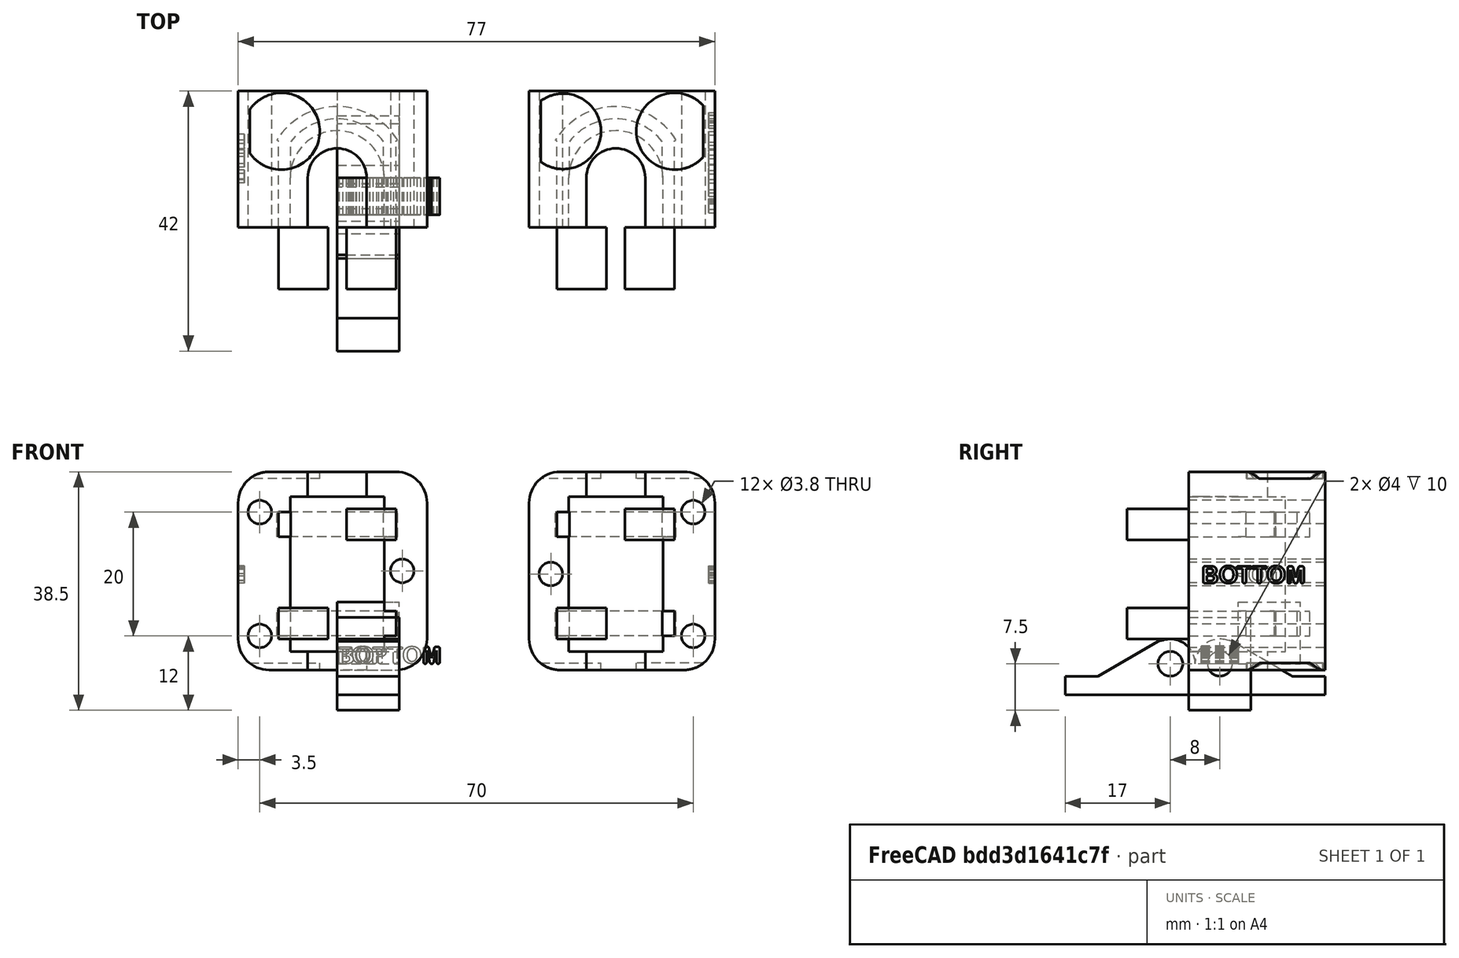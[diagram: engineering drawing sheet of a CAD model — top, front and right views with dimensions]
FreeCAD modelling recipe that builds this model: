
FCSTD DOCUMENT  (FreeCAD 0.16R6712 (Git))
Label: ParkingNozzleSliderIron
License: All rights reserved
LicenseURL: http://en.wikipedia.org/wiki/All_rights_reserved
objects: Part::Cylinder×51, Part::Box×26, Part::MultiFuse×26, Part::Cut×17, Part::Feature×3, Part::Part2DObjectPython×2, Part::Extrusion×2
note: 127 computed .brp shape members not serialized (recipe doc carries the construction recipe); baked Part::Feature solids carry a one-line shape summary decoded from their .brp

FEATURE [Part::Box] Box  label="Würfel"
  Height = 10
  Length = 10
  Width = 10
FEATURE [Part::Cylinder] Cylinder001  label="RJ4JP"
  Angle = 360
  Height = 25
  Placement = pos=(0,0,-0.5) rot=(0,0,1;0rad)
  Radius = 7.6
FEATURE [Part::Cylinder] Cylinder002  label="LinearStange8mm"
  Angle = 360
  Height = 44
  Placement = pos=(0,0,-10) rot=(0,0,1;0rad)
  Radius = 4.5
FEATURE [Part::Cylinder] Cylinder003  label="LinearSpacer9mm"
  Angle = 360
  Height = 34
  Placement = pos=(0,0,-5) rot=(0,0,1;0rad)
  Radius = 4.75
FEATURE [Part::MultiFuse] Fusion  label="GleitlagerAusspahrung"
  Shapes = -> [Cylinder001,Cylinder003,Cylinder002]
FEATURE [Part::Cylinder] Cylinder004  label="Zylinder001"
  Angle = 116
  Height = 4
  Placement = pos=(0,0,0) rot=(0,0,1;0.558505rad)
  Radius = 11.5
FEATURE [Part::Cylinder] Cylinder005  label="Zylinder002"
  Angle = 116
  Height = 4
  Placement = pos=(0,0,0) rot=(0,0,1;0.558505rad)
  Radius = 9.5
FEATURE [Part::Cut] Cut
  Base = -> Cylinder004
  Tool = -> Cylinder005
FEATURE [Part::Box] Box001  label="Würfel001"
  Height = 4
  Length = 2
  Placement = pos=(-9.5,-11,0) rot=(0,0,1;0rad)
  Width = 17
FEATURE [Part::Box] Box002  label="Würfel002"
  Height = 4
  Length = 2
  Placement = pos=(7.5,-11,0) rot=(0,0,1;0rad)
  Width = 17
FEATURE [Part::MultiFuse] Fusion001  label="KabelbinderAusspahrung002"
  Placement = pos=(0,0,18) rot=(0,0,1;0rad)
  Shapes = -> [Cut,Box002,Box001]
FEATURE [Part::Box] Box009  label="Würfel009"
  Height = 15
  Length = 10
  Placement = pos=(0,-8,-7.5) rot=(0,0,1;0rad)
  Width = 10
FEATURE [Part::Cylinder] Cylinder014  label="Zylinder008"
  Angle = 116
  Height = 4
  Placement = pos=(0,0,0) rot=(0,0,1;0.558505rad)
  Radius = 11.5
FEATURE [Part::Cylinder] Cylinder015  label="Zylinder009"
  Angle = 116
  Height = 4
  Placement = pos=(0,0,0) rot=(0,0,1;0.558505rad)
  Radius = 9.5
FEATURE [Part::Cut] Cut004
  Base = -> Cylinder014
  Tool = -> Cylinder015
FEATURE [Part::Box] Box010  label="Würfel010"
  Height = 4
  Length = 2
  Placement = pos=(-9.5,-11,0) rot=(0,0,1;0rad)
  Width = 17
FEATURE [Part::Box] Box011  label="Würfel011"
  Height = 4
  Length = 2
  Placement = pos=(7.5,-11,0) rot=(0,0,1;0rad)
  Width = 17
FEATURE [Part::MultiFuse] Fusion008  label="KabelbinderAusspahrung005"
  Placement = pos=(0,0,2) rot=(0,0,1;0rad)
  Shapes = -> [Cut004,Box011,Box010]
FEATURE [Part::Box] Box016  label="Block_A"
  Height = 32
  Length = 30.5
  Placement = pos=(-16,-8,-1) rot=(0,0,1;0rad)
  Width = 22
FEATURE [Part::Box] Box017  label="Würfel017"
  Height = 44
  Length = 9.5
  Placement = pos=(-4.75,-11,-10) rot=(0,0,1;0rad)
  Width = 11
FEATURE [Part::Box] Box018  label="Würfel018"
  Height = 25
  Length = 15.2
  Placement = pos=(-7.6,-11,-0.5) rot=(0,0,1;0rad)
  Width = 11
FEATURE [Part::MultiFuse] Fusion014  label="Schacht"
  Shapes = -> [Box017,Box018]
FEATURE [Part::MultiFuse] Fusion015  label="RJ4JP_Cut_Full_A"
  Shapes = -> [Fusion,Fusion001,Fusion008,Fusion014]
FEATURE [Part::Cylinder] Cylinder016  label="RJ4JP001"
  Angle = 360
  Height = 25
  Placement = pos=(0,0,-0.5) rot=(0,0,1;0rad)
  Radius = 7.6
FEATURE [Part::Cylinder] Cylinder017  label="LinearStange8mm001"
  Angle = 360
  Height = 44
  Placement = pos=(0,0,-10) rot=(0,0,1;0rad)
  Radius = 4.5
FEATURE [Part::Cylinder] Cylinder018  label="LinearSpacer9mm001"
  Angle = 360
  Height = 34
  Placement = pos=(0,0,-5) rot=(0,0,1;0rad)
  Radius = 4.75
FEATURE [Part::MultiFuse] Fusion016  label="GleitlagerAusspahrung001"
  Shapes = -> [Cylinder016,Cylinder018,Cylinder017]
FEATURE [Part::Cylinder] Cylinder019  label="Zylinder010"
  Angle = 116
  Height = 4
  Placement = pos=(0,0,0) rot=(0,0,1;0.558505rad)
  Radius = 11.5
FEATURE [Part::Cylinder] Cylinder020  label="Zylinder011"
  Angle = 116
  Height = 4
  Placement = pos=(0,0,0) rot=(0,0,1;0.558505rad)
  Radius = 9.5
FEATURE [Part::Cut] Cut005
  Base = -> Cylinder019
  Tool = -> Cylinder020
FEATURE [Part::Box] Box019  label="Würfel019"
  Height = 4
  Length = 2
  Placement = pos=(-9.5,-11,0) rot=(0,0,1;0rad)
  Width = 17
FEATURE [Part::Box] Box020  label="Würfel020"
  Height = 4
  Length = 2
  Placement = pos=(7.5,-11,0) rot=(0,0,1;0rad)
  Width = 17
FEATURE [Part::MultiFuse] Fusion017  label="KabelbinderAusspahrung006"
  Placement = pos=(0,0,18) rot=(0,0,1;0rad)
  Shapes = -> [Cut005,Box020,Box019]
FEATURE [Part::Cylinder] Cylinder021  label="Zylinder012"
  Angle = 116
  Height = 4
  Placement = pos=(0,0,0) rot=(0,0,1;0.558505rad)
  Radius = 11.5
FEATURE [Part::Cylinder] Cylinder022  label="Zylinder013"
  Angle = 116
  Height = 4
  Placement = pos=(0,0,0) rot=(0,0,1;0.558505rad)
  Radius = 9.5
FEATURE [Part::Cut] Cut006
  Base = -> Cylinder021
  Tool = -> Cylinder022
FEATURE [Part::Box] Box021  label="Würfel021"
  Height = 4
  Length = 2
  Placement = pos=(-9.5,-11,0) rot=(0,0,1;0rad)
  Width = 17
FEATURE [Part::Box] Box022  label="Würfel022"
  Height = 4
  Length = 2
  Placement = pos=(7.5,-11,0) rot=(0,0,1;0rad)
  Width = 17
FEATURE [Part::MultiFuse] Fusion018  label="KabelbinderAusspahrung007"
  Placement = pos=(0,0,2) rot=(0,0,1;0rad)
  Shapes = -> [Cut006,Box022,Box021]
FEATURE [Part::Box] Box023  label="Würfel023"
  Height = 44
  Length = 9.5
  Placement = pos=(-4.75,-11,-10) rot=(0,0,1;0rad)
  Width = 11
FEATURE [Part::Box] Box024  label="Würfel024"
  Height = 25
  Length = 15.2
  Placement = pos=(-7.6,-11,-0.5) rot=(0,0,1;0rad)
  Width = 11
FEATURE [Part::MultiFuse] Fusion019  label="Schacht001"
  Shapes = -> [Box023,Box024]
FEATURE [Part::MultiFuse] Fusion020  label="RJ4JP_Cut_Full_B"
  Placement = pos=(45,0,0) rot=(0,0,1;0rad)
  Shapes = -> [Fusion016,Fusion017,Fusion018,Fusion019]
FEATURE [Part::MultiFuse] Fusion021  label="X_RJ4JP_Cut"
  Placement = pos=(0,0,2.5) rot=(0,0,1;0rad)
  Shapes = -> [Fusion015,Fusion020]
FEATURE [Part::Box] Box025  label="Block_B"
  Height = 32
  Length = 30
  Placement = pos=(31,-8,-1) rot=(0,0,1;0rad)
  Width = 22
FEATURE [Part::MultiFuse] Fusion022  label="GleitBlock"
  Shapes = -> [Box016,Box025]
FEATURE [Part::Cut] Cut007  label="GleitBloecke"
  Base = -> Fusion022
  Tool = -> Fusion021
FEATURE [Part::Cylinder] Cylinder025  label="Zylinder016"
  Angle = 360
  Height = 10
  Radius = 2
FEATURE [Part::Cylinder] Cylinder026  label="Zylinder017"
  Angle = 360
  Height = 10
  Radius = 4
FEATURE [Part::Cut] Cut009
  Base = -> Cylinder026
  Placement = pos=(0,-11,0) rot=(0,0,1;0rad)
  Tool = -> Cylinder025
FEATURE [Part::Box] Box028  label="Würfel027"
  Height = 10
  Length = 3
  Placement = pos=(2,-28,0) rot=(0,0,1;0rad)
  Width = 22
FEATURE [Part::Box] Box029  label="Würfel028"
  Height = 10
  Length = 1
  Placement = pos=(3.9,-26,0) rot=(0,0,1;0.523599rad)
  Width = 15
FEATURE [Part::Box] Box030  label="Würfel029"
  Height = 10
  Length = 3.3
  Placement = pos=(2,-21.5,0) rot=(0,0,1;0.523599rad)
  Width = 8
FEATURE [Part::Cylinder] Cylinder027  label="Zylinder018"
  Angle = 360
  Height = 10
  Placement = pos=(2,-15,0) rot=(0,0,1;0rad)
  Radius = 2
FEATURE [Part::Cylinder] Cylinder028  label="Zylinder019"
  Angle = 360
  Height = 10
  Placement = pos=(-2.73,-12.5,0) rot=(0,0,1;0rad)
  Radius = 1
FEATURE [Part::MultiFuse] Fusion023
  Shapes = -> [Cut009,Cylinder027,Cylinder028,Box028,Box029,Box030]
FEATURE [Part::Cylinder] Cylinder029  label="Zylinder020"
  Angle = 360
  Height = 10
  Radius = 2
FEATURE [Part::Cylinder] Cylinder030  label="Zylinder021"
  Angle = 360
  Height = 10
  Radius = 4
FEATURE [Part::Cut] Cut010
  Base = -> Cylinder030
  Placement = pos=(0,-11,0) rot=(0,0,1;0rad)
  Tool = -> Cylinder029
FEATURE [Part::Box] Box031  label="Würfel030"
  Height = 10
  Length = 3
  Placement = pos=(2,-28,0) rot=(0,0,1;0rad)
  Width = 20
FEATURE [Part::Box] Box032  label="Würfel031"
  Height = 10
  Length = 1
  Placement = pos=(3.9,-26,0) rot=(0,0,1;0.523599rad)
  Width = 15
FEATURE [Part::Box] Box033  label="Würfel032"
  Height = 10
  Length = 3.3
  Placement = pos=(2,-21.5,0) rot=(0,0,1;0.523599rad)
  Width = 8
FEATURE [Part::Cylinder] Cylinder031  label="Zylinder022"
  Angle = 360
  Height = 10
  Placement = pos=(2,-15,0) rot=(0,0,1;0rad)
  Radius = 2
FEATURE [Part::Cylinder] Cylinder032  label="Zylinder023"
  Angle = 360
  Height = 10
  Placement = pos=(-2.73,-12.5,0) rot=(0,0,1;0rad)
  Radius = 1
FEATURE [Part::MultiFuse] Fusion024
  Placement = pos=(0,-14,10) rot=(1,0,0;3.14159rad)
  Shapes = -> [Cut010,Cylinder031,Cylinder032,Box031,Box032,Box033]
FEATURE [Part::MultiFuse] Fusion025
  Shapes = -> [Fusion023,Fusion024]
FEATURE [Part::Cylinder] Cylinder033  label="Zylinder024"
  Angle = 360
  Height = 10
  Placement = pos=(2,-7,0) rot=(0,0,1;0rad)
  Radius = 2
FEATURE [Part::MultiFuse] Fusion026
  Placement = pos=(0,0,0) rot=(0,1,0;1.5708rad)
  Shapes = -> [Fusion025,Cylinder033]
FEATURE [Part::Cylinder] Cylinder034  label="Zylinder025"
  Angle = 360
  Height = 26
  Placement = pos=(-13,16,4.5) rot=(1,0,0;1.5708rad)
  Radius = 1.9
FEATURE [Part::Cylinder] Cylinder035  label="Zylinder026"
  Angle = 360
  Height = 26
  Placement = pos=(-13,16,24.5) rot=(1,0,0;1.5708rad)
  Radius = 1.9
FEATURE [Part::Cylinder] Cylinder036  label="Zylinder027"
  Angle = 360
  Height = 26
  Placement = pos=(10.5,16,15) rot=(1,0,0;1.5708rad)
  Radius = 1.9
FEATURE [Part::MultiFuse] Fusion026003
  Placement = pos=(0.5,0,0) rot=(0,0,1;0rad)
  Shapes = -> [Cylinder034,Cylinder035]
FEATURE [Part::Cylinder] Cylinder037  label="Zylinder028"
  Angle = 360
  Height = 26
  Placement = pos=(-13,16,4.5) rot=(1,0,0;1.5708rad)
  Radius = 1.9
FEATURE [Part::Cylinder] Cylinder038  label="Zylinder029"
  Angle = 360
  Height = 26
  Placement = pos=(-13,16,24.5) rot=(1,0,0;1.5708rad)
  Radius = 1.9
FEATURE [Part::MultiFuse] Fusion026004
  Placement = pos=(70.5,0,0) rot=(0,0,1;0rad)
  Shapes = -> [Cylinder037,Cylinder038]
FEATURE [Part::Cylinder] Cylinder039  label="Zylinder030"
  Angle = 360
  Height = 26
  Placement = pos=(34.5,16,14.5) rot=(1,0,0;1.5708rad)
  Radius = 1.9
FEATURE [Part::MultiFuse] Fusion026005  label="Bohrung"
  Shapes = -> [Cylinder036,Fusion026003,Fusion026004,Cylinder039]
FEATURE [Part::Part2DObjectPython] ShapeString  # Draft 2D object (typed FeaturePython)
  FontFile = <path>
  Size = 3
  String = TOP
  Tracking = 4
FEATURE [Part::Extrusion] Extrude
  Base = -> ShapeString
  Dir = (0,0,6)
  Placement = pos=(0,0,0) rot=(1,0,0;1.5708rad)
  Solid = false
FEATURE [Part::Part2DObjectPython] ShapeString001  # Draft 2D object (typed FeaturePython)
  FontFile = <path>
  Size = 3
  String = BOTTOM
  Tracking = 4
FEATURE [Part::Extrusion] Extrude001
  Base = -> ShapeString001
  Dir = (0,0,6)
  Placement = pos=(0,0,0) rot=(1,0,0;1.5708rad)
  Solid = false
FEATURE [Part::Feature] Extrude002
  Placement = pos=(-15,7,13) rot=(0,0,-1;1.5708rad)
  shape: bbox 6 x 7.877 x 2.835 mm, 76 faces, 3 solids (baked)
FEATURE [Part::Feature] Extrude001001  label="Extrude003"
  Placement = pos=(60,-6,13) rot=(0,0,1;1.5708rad)
  shape: bbox 6 x 16.23 x 2.835 mm, 171 faces, 6 solids (baked)
FEATURE [Part::MultiFuse] Fusion026006
  Shapes = -> [Extrude002,Extrude001001]
FEATURE [Part::Cut] Cut011002  label="Bloecke"
  Base = -> Cut007
  Tool = -> Fusion026006
FEATURE [Part::Cylinder] Cylinder041  label="Zylinder032"
  Angle = 360
  Height = 1.1
  Placement = pos=(-9,0,0) rot=(0,0,1;0rad)
  Radius = 6.2
FEATURE [Part::Cylinder] Cylinder042  label="Zylinder033"
  Angle = 360
  Height = 1.1
  Placement = pos=(54.5,0,0) rot=(0,0,1;0rad)
  Radius = 6.2
FEATURE [Part::Cylinder] Cylinder043  label="Zylinder034"
  Angle = 360
  Height = 1.1
  Placement = pos=(36.5,0,0) rot=(0,0,1;0rad)
  Radius = 6.1
FEATURE [Part::MultiFuse] Fusion026009  label="MagnetsLeft"
  Placement = pos=(0,7.5,29.9) rot=(0,0,1;0rad)
  Shapes = -> [Cylinder041,Cylinder043,Cylinder042]
FEATURE [Part::Cylinder] Cylinder044  label="Zylinder035"
  Angle = 360
  Height = 1.1
  Placement = pos=(-9,0,0) rot=(0,0,1;0rad)
  Radius = 6.2
FEATURE [Part::Cylinder] Cylinder045  label="Zylinder036"
  Angle = 360
  Height = 1.1
  Placement = pos=(54.5,0,0) rot=(0,0,1;0rad)
  Radius = 6.2
FEATURE [Part::Cylinder] Cylinder046  label="Zylinder037"
  Angle = 360
  Height = 1.1
  Placement = pos=(36.5,0,0) rot=(0,0,1;0rad)
  Radius = 6.1
FEATURE [Part::MultiFuse] Fusion026010  label="MagnetsRight"
  Placement = pos=(0,7.5,-1) rot=(0,0,1;0rad)
  Shapes = -> [Cylinder044,Cylinder046,Cylinder045]
FEATURE [Part::MultiFuse] Fusion026011  label="Magnets"
  Shapes = -> [Fusion026009,Fusion026010]
FEATURE [Part::Cylinder] Cylinder047  label="Zylinder038"
  Angle = 90
  Height = 40
  Placement = pos=(33,25,29) rot=(1,0,0;1.5708rad)
  Radius = 8
FEATURE [Part::Cylinder] Cylinder048  label="Zylinder039"
  Angle = 90
  Height = 40
  Placement = pos=(33,25,29) rot=(1,0,0;1.5708rad)
  Radius = 5
FEATURE [Part::Cut] Cut011004002
  Base = -> Cylinder047
  Placement = pos=(65,0,-7) rot=(0,-1,0;1.5708rad)
  Tool = -> Cylinder048
FEATURE [Part::Cylinder] Cylinder049  label="Zylinder040"
  Angle = 90
  Height = 40
  Placement = pos=(33,25,29) rot=(1,0,0;1.5708rad)
  Radius = 8
FEATURE [Part::Cylinder] Cylinder050  label="Zylinder041"
  Angle = 90
  Height = 40
  Placement = pos=(33,25,29) rot=(1,0,0;1.5708rad)
  Radius = 5
FEATURE [Part::Cut] Cut011004003
  Base = -> Cylinder049
  Placement = pos=(69,0,33) rot=(0,1,0;3.14159rad)
  Tool = -> Cylinder050
FEATURE [Part::Cylinder] Cylinder051  label="Zylinder042"
  Angle = 90
  Height = 40
  Placement = pos=(33,25,29) rot=(1,0,0;1.5708rad)
  Radius = 8
FEATURE [Part::Cylinder] Cylinder052  label="Zylinder043"
  Angle = 90
  Height = 40
  Placement = pos=(33,25,29) rot=(1,0,0;1.5708rad)
  Radius = 5
FEATURE [Part::Cut] Cut011004004
  Base = -> Cylinder051
  Placement = pos=(18,0,-7) rot=(0,-1,0;1.5708rad)
  Tool = -> Cylinder052
FEATURE [Part::Cylinder] Cylinder053  label="Zylinder044"
  Angle = 90
  Height = 40
  Placement = pos=(33,25,29) rot=(1,0,0;1.5708rad)
  Radius = 8
FEATURE [Part::Cylinder] Cylinder054  label="Zylinder045"
  Angle = 90
  Height = 40
  Placement = pos=(33,25,29) rot=(1,0,0;1.5708rad)
  Radius = 5
FEATURE [Part::Cut] Cut011004005
  Base = -> Cylinder053
  Placement = pos=(22,0,33) rot=(0,1,0;3.14159rad)
  Tool = -> Cylinder054
FEATURE [Part::Cylinder] Cylinder055  label="Zylinder046"
  Angle = 90
  Height = 40
  Placement = pos=(33,25,29) rot=(1,0,0;1.5708rad)
  Radius = 8
FEATURE [Part::Cylinder] Cylinder056  label="Zylinder047"
  Angle = 90
  Height = 40
  Placement = pos=(33,25,29) rot=(1,0,0;1.5708rad)
  Radius = 5
FEATURE [Part::Cut] Cut011004006
  Base = -> Cylinder055
  Placement = pos=(23,0,-3) rot=(0,0,1;0rad)
  Tool = -> Cylinder056
FEATURE [Part::Cylinder] Cylinder057  label="Zylinder048"
  Angle = 90
  Height = 40
  Placement = pos=(33,25,29) rot=(1,0,0;1.5708rad)
  Radius = 8
FEATURE [Part::Cylinder] Cylinder058  label="Zylinder049"
  Angle = 90
  Height = 40
  Placement = pos=(33,25,29) rot=(1,0,0;1.5708rad)
  Radius = 5
FEATURE [Part::Cut] Cut011004007
  Base = -> Cylinder057
  Placement = pos=(-19.5,0,37) rot=(0,1,0;1.5708rad)
  Tool = -> Cylinder058
FEATURE [Part::Cylinder] Cylinder059  label="Zylinder050"
  Angle = 90
  Height = 40
  Placement = pos=(33,25,29) rot=(1,0,0;1.5708rad)
  Radius = 8
FEATURE [Part::Cylinder] Cylinder060  label="Zylinder051"
  Angle = 90
  Height = 40
  Placement = pos=(33,25,29) rot=(1,0,0;1.5708rad)
  Radius = 5
FEATURE [Part::Cut] Cut011004008
  Base = -> Cylinder059
  Placement = pos=(27,0,37) rot=(0,1,0;1.5708rad)
  Tool = -> Cylinder060
FEATURE [Part::Cylinder] Cylinder061  label="Zylinder052"
  Angle = 90
  Height = 40
  Placement = pos=(33,25,29) rot=(1,0,0;1.5708rad)
  Radius = 8
FEATURE [Part::Cylinder] Cylinder062  label="Zylinder053"
  Angle = 90
  Height = 40
  Placement = pos=(33,25,29) rot=(1,0,0;1.5708rad)
  Radius = 5
FEATURE [Part::Cut] Cut011004009
  Base = -> Cylinder061
  Placement = pos=(-23.5,0,-3) rot=(0,0,1;0rad)
  Tool = -> Cylinder062
FEATURE [Part::MultiFuse] Fusion026012  label="RoundEdges"
  Shapes = -> [Cut011004002,Cut011004003,Cut011004009,Cut011004008,Cut011004006,Cut011004007,Cut011004004,Cut011004005]
FEATURE [Part::MultiFuse] Fusion026014  label="To_Cut"
  Shapes = -> [Fusion026012,Fusion026011,Fusion026005]
FEATURE [Part::Cut] Cut011004010  label="NozzleSliderIron"
  Base = -> Cut011002
  Tool = -> Fusion026014
FEATURE [Part::Box] Box034  label="Würfel033"
  Height = 5
  Length = 8
  Placement = pos=(-9.5,-18,4) rot=(0,0,1;0rad)
  Width = 10
FEATURE [Part::Box] Box035  label="Würfel034"
  Height = 5
  Length = 8
  Placement = pos=(35.5,-18,4) rot=(0,0,1;0rad)
  Width = 10
FEATURE [Part::Box] Box036  label="Würfel035"
  Height = 5
  Length = 8
  Placement = pos=(1.5,-18,20) rot=(0,0,1;0rad)
  Width = 10
FEATURE [Part::Box] Box037  label="Würfel036"
  Height = 5
  Length = 8
  Placement = pos=(46.5,-18,20) rot=(0,0,1;0rad)
  Width = 10
FEATURE [Part::MultiFuse] Fusion026015  label="SripperHoles"
  Shapes = -> [Box034,Box037,Box035,Box036]
FEATURE [Part::Feature] Cut011004010001  label="NozzleSliderIron_export"
  shape: bbox 77 x 22 x 32 mm, 354 faces, 2 solids (baked)
note: 2 file-system paths scrubbed to <path> (originals preserved in the JSON sidecar)
